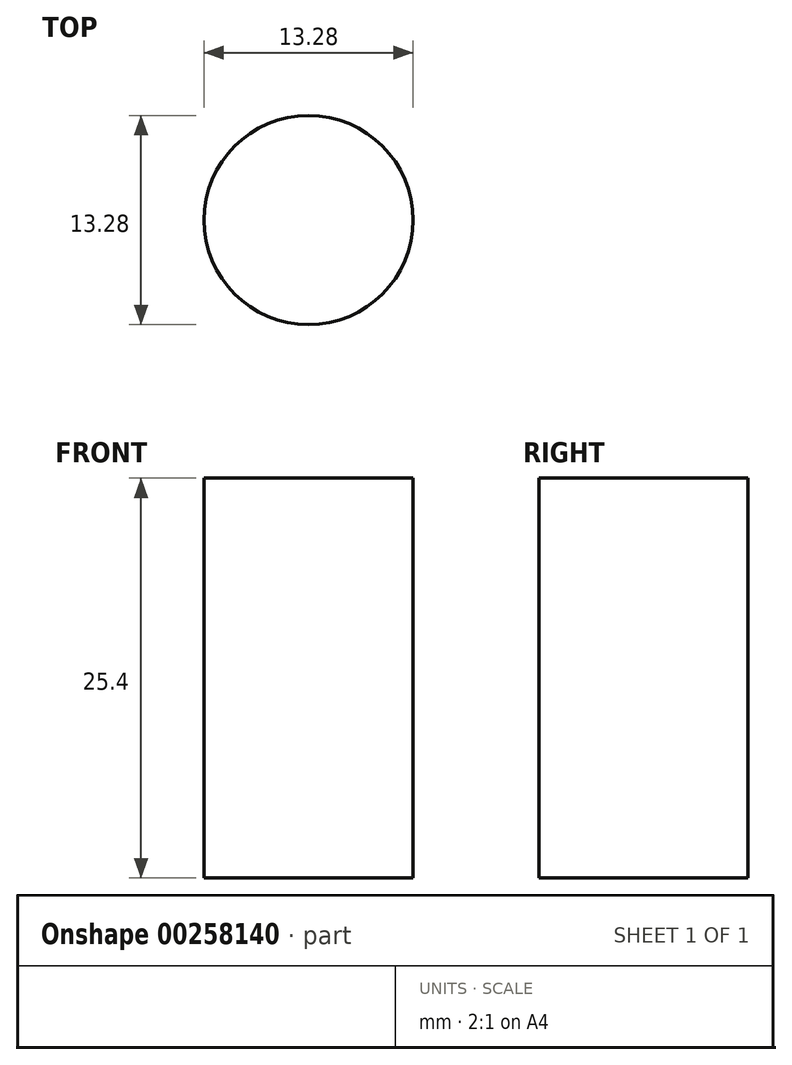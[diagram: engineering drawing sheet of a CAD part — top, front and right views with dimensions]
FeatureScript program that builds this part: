
annotation { "Feature Type Name" : "Feature", "Feature Type Description" : "" }
export const myFeature = defineFeature(function(context is Context, id is Id, definition is map)
    precondition{}
    {
        {
            var Q0;
            Q0=qCreatedBy(makeId("Top.planeOp"),FACE);
            var sketch = newSketch(context, id + "F0", { "sketchPlane" : qUnion([Q0])});
            skCircle(sketch, "E0", {"center": v(0, 0) * mm, "radius": 6.64 * mm});
            skSolve(sketch);
        }
        {
            var Q0;
            Q0=makeQuery(id+"F0.imprint","IMPRINT",FACE,{"disambiguationData":[TD([[makeQuery(id+"F0.imprint","IMPRINT",EDGE,{"derivedFrom":sQuery(id+"F0.wireOp",EDGE,"E0")}),1.0]])]});
            extrude(context, id + "F1", {"entities" : qUnion([Q0]), "depth" : 25.4 * mm});
        }
    });
